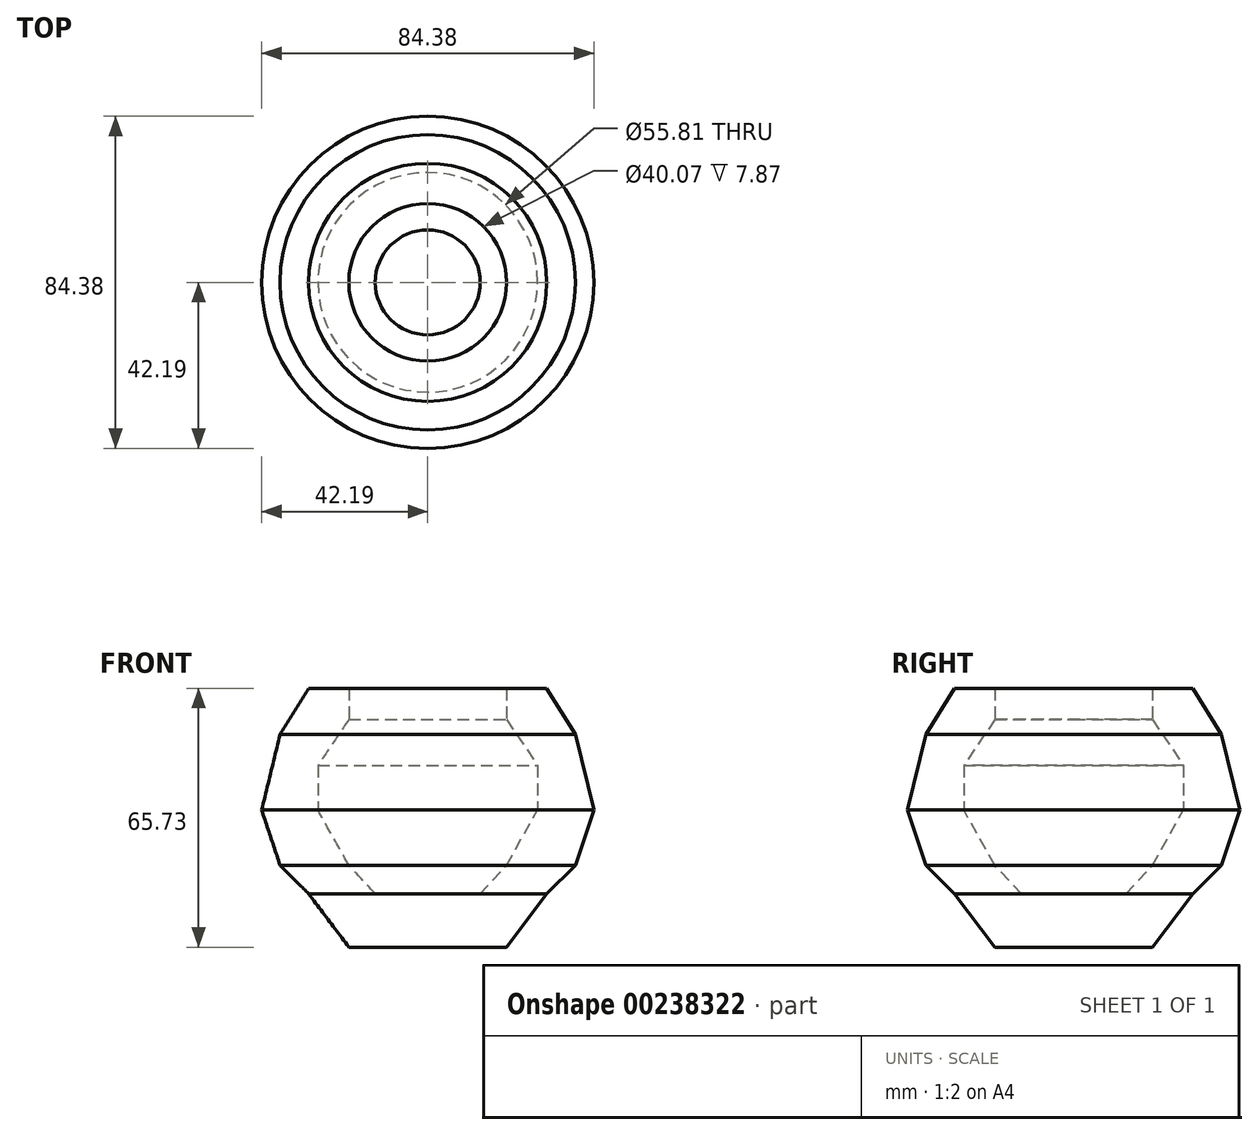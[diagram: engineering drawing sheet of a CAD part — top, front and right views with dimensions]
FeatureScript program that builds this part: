
annotation { "Feature Type Name" : "Feature", "Feature Type Description" : "" }
export const myFeature = defineFeature(function(context is Context, id is Id, definition is map)
    precondition{}
    {
        {
            var Q0;
            Q0=qCreatedBy(makeId("Right.planeOp"),FACE);
            var sketch = newSketch(context, id + "F0", { "sketchPlane" : qUnion([Q0])});
            skLineSegment(sketch, "E0", {"start": v(0, 0) * mm, "end": v(0, 75.05) * mm, "construction": true});
            skLineSegment(sketch, "E1", {"start": v(0, 0) * mm, "end": v(0, 13.55) * mm});
            skLineSegment(sketch, "E2", {"start": v(0, 13.55) * mm, "end": v(-13.33, 13.55) * mm});
            skLineSegment(sketch, "E3", {"start": v(-13.33, 13.55) * mm, "end": v(-20.03, 20.84) * mm});
            skLineSegment(sketch, "E4", {"start": v(-20.03, 20.84) * mm, "end": v(-27.9, 34.83) * mm});
            skLineSegment(sketch, "E5", {"start": v(-27.9, 34.83) * mm, "end": v(-27.9, 46.2) * mm});
            skLineSegment(sketch, "E6", {"start": v(-27.9, 46.2) * mm, "end": v(-20.03, 57.86) * mm});
            skLineSegment(sketch, "E7", {"start": v(-20.03, 57.86) * mm, "end": v(-20.03, 65.73) * mm});
            skLineSegment(sketch, "E8", {"start": v(-20.03, 65.73) * mm, "end": v(-30.23, 65.73) * mm});
            skLineSegment(sketch, "E9", {"start": v(-30.23, 65.73) * mm, "end": v(-37.52, 54.07) * mm});
            skLineSegment(sketch, "E10", {"start": v(-37.52, 54.07) * mm, "end": v(-42.19, 34.83) * mm});
            skLineSegment(sketch, "E11", {"start": v(-42.19, 34.83) * mm, "end": v(-37.52, 20.84) * mm});
            skLineSegment(sketch, "E12", {"start": v(-37.52, 20.84) * mm, "end": v(-30.23, 13.55) * mm});
            skLineSegment(sketch, "E13", {"start": v(-30.23, 13.55) * mm, "end": v(-20.03, 0) * mm});
            skLineSegment(sketch, "E14", {"start": v(-20.03, 0) * mm, "end": v(0, 0) * mm});
            skSolve(sketch);
        }
        {
            var Q0;
            Q0 = qSketchRegion(id + "F0", true);
            var Q1;
            Q1=sQuery(id+"F0.wireOp",EDGE,"E0");
            revolve(context, id + "F1", {"entities" : qUnion([Q0]), "axis" : qUnion([Q1]), "revolveType" : RevolveType.FULL});
        }
    });
